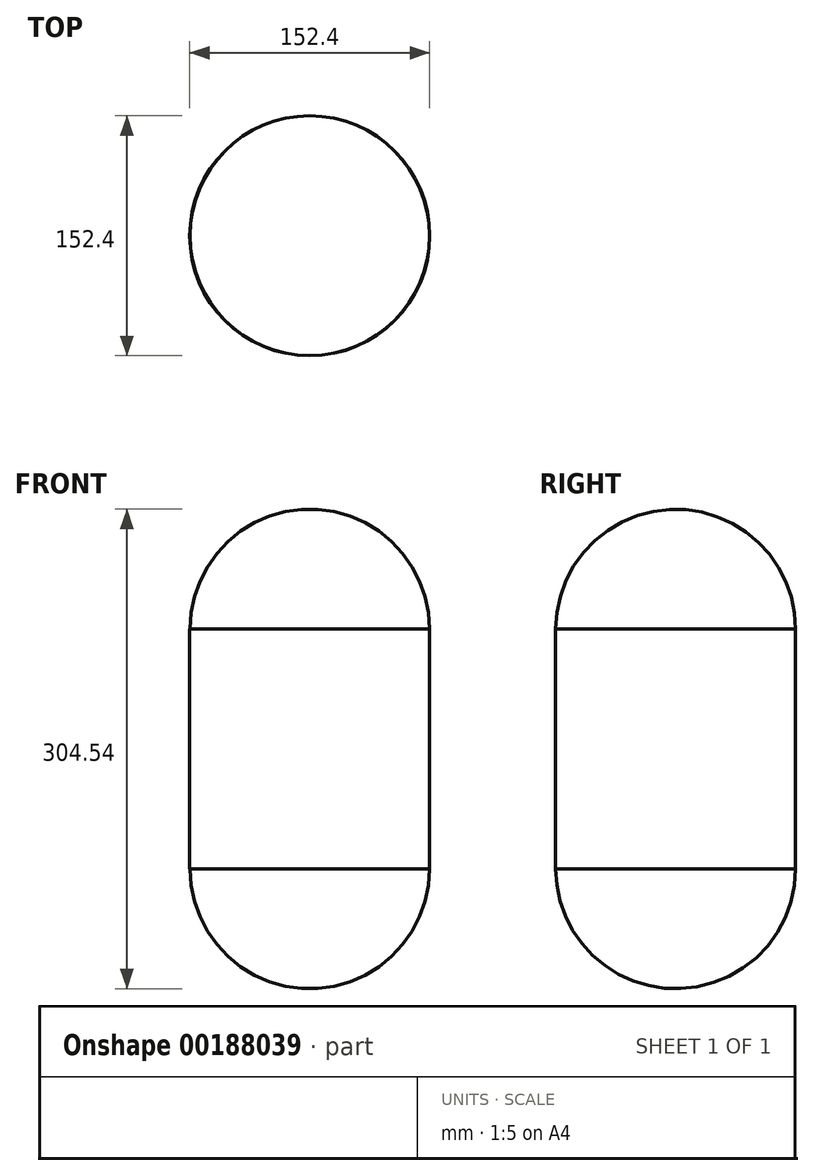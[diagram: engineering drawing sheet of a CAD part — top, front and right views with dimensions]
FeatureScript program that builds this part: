
annotation { "Feature Type Name" : "Feature", "Feature Type Description" : "" }
export const myFeature = defineFeature(function(context is Context, id is Id, definition is map)
    precondition{}
    {
        {
            var Q0;
            Q0=qCreatedBy(makeId("Front.planeOp"),FACE);
            var sketch = newSketch(context, id + "F0", { "sketchPlane" : qUnion([Q0])});
            skLineSegment(sketch, "E0.bottom", {"start": v(0, 0) * mm, "end": v(-76.2, 0) * mm});
            skLineSegment(sketch, "E0.top", {"start": v(0, 76.2) * mm, "end": v(-76.2, 76.2) * mm});
            skLineSegment(sketch, "E0.left", {"start": v(0, 0) * mm, "end": v(0, 76.2) * mm});
            skLineSegment(sketch, "E0.right", {"start": v(-76.2, 0) * mm, "end": v(-76.2, 76.2) * mm});
            skSolve(sketch);
        }
        {
            var Q0;
            Q0 = qSketchRegion(id + "F0", true);
            var Q1;
            Q1=sQuery(id+"F0.wireOp",EDGE,"E0.left");
            revolve(context, id + "F1", {"entities" : qUnion([Q0]), "axis" : qUnion([Q1]), "revolveType" : RevolveType.FULL});
        }
        {
            var Q0;
            Q0=makeQuery(id+"F1.opRevolve","SWEPT_FACE",FACE,{"disambiguationData":[OSD([sQuery(id+"F0.wireOp",EDGE,"E0.bottom")])]});
            var sketch = newSketch(context, id + "F2", { "sketchPlane" : qUnion([Q0])});
            skArc(sketch, "E1", {"start": v(0, 76.2) * mm, "mid": v(-76.07, 0) * mm, "end": v(0, -76.2) * mm});
            skLineSegment(sketch, "E2", {"start": v(0, 76.2) * mm, "end": v(0, -76.2) * mm});
            skSolve(sketch);
        }
        {
            var Q0;
            Q0 = qSketchRegion(id + "F2", true);
            var Q1;
            Q1=sQuery(id+"F2.wireOp",EDGE,"E2");
            revolve(context, id + "F3", {"operationType" : NewBodyOperationType.ADD, "entities" : qUnion([Q0]), "axis" : qUnion([Q1]), "revolveType" : RevolveType.FULL});
        }
        {
            var Q0;
            Q0=makeQuery(id+"F1.opRevolve","SWEPT_BODY",BODY,{"disambiguationData":[OSD([sQuery(id+"F0.wireOp",EDGE,"E0.bottom"),sQuery(id+"F0.wireOp",EDGE,"E0.top"),sQuery(id+"F0.wireOp",EDGE,"E0.left"),sQuery(id+"F0.wireOp",EDGE,"E0.right")])]});
            var Q1;
            Q1=makeQuery(id+"F1.opRevolve","SWEPT_FACE",FACE,{"disambiguationData":[OSD([sQuery(id+"F0.wireOp",EDGE,"E0.top")])]});
            mirror(context, id + "F4", {"operationType" : NewBodyOperationType.ADD, "entities" : qUnion([Q0]), "mirrorPlane" : qUnion([Q1])});
        }
    });
